# Revit family: Faucet-Lavatory-KOHLER-Forte-K-10270_1
name_source: partatom
category: Plumbing Fixtures
revit_build: Autodesk Revit 2015 (Build: 20140606_1530(x64)
units: mm (PartAtom-declared; Revit-internal decimal feet)

## types (6) — shared parameters
ADA Compliant = Yes
Assembly Code = D2010
CW Connection = Yes
Cold Water Inlet = Cold Water Inlet
Date Modified = 02/20/2019
Default Elevation = 36"
Drain Included = Yes
Faucet Hole Spacing = 4"
HW Connection = Yes
Handle Clearance = 2 9/16"
Height = 4 13/16"
Hot Water Inlet = Hot Water Inlet
Length = 5 1/8"
Manufacturer = KOHLER Co.
MasterFormat 1995 = 15410
MasterFormat 2004 = 22.41.39
Material = Premium Metal Construction
Pressure = 60.00 psi
Product Documentation Link = https://www.us.kohler.com
Product Name = Forté
Product Page URL = http://www.us.kohler.com
Spout Reach = 5 1/8"
URL = https://www.us.kohler.com
Vent Connection = No
Waste Connection = No
Waste Water Outlet = Waste Water Outlet
WaterSense Certified = Yes
Width = 4"

## per-type parameters (varying)
| type | Description | Finish | Flow Rate | Model | Sculpted Lever Handles | Traditional Lever Handles | Type |
| Sculpted Lever Handle, CP-Polished Chrome | Centerset bathroom sink faucet with sculpted lever handles | Kohler-Metal-CP-Polished_Chrome | 1 GPM | K-10270-4-CP | Yes | No | 1 |
| Sculpted Lever Handle, G-Brushed Chrome | Centerset bathroom sink faucet with sculpted lever handles | Kohler-Metal-G-Brushed_Chrome | 1 GPM | K-10270-4-G | Yes | No | 2 |
| Sculpted Lever Handle, BN-Vibrant Brushed Nickel | Centerset bathroom sink faucet with sculpted lever handles | Kohler-Metal-BN-Vibrant_Brushed_Nickel | 1 GPM | K-10270-4-BN | Yes | No | 3 |
| Traditional Lever Handle, CP-Polished Chrome | Centerset bathroom sink faucet with traditional lever handles | Kohler-Metal-CP-Polished_Chrome | 2 GPM | K-10270-4A-CP | No | Yes | 4 |
| Traditional Lever Handle, G-Brushed Chrome | Centerset bathroom sink faucet with traditional lever handles | Kohler-Metal-G-Brushed_Chrome | 2 GPM | K-10270-4A-G | No | Yes | 5 |
| Traditional Lever Handle, BN-Vibrant Brushed Nickel | Centerset bathroom sink faucet with traditional lever handles | Kohler-Metal-BN-Vibrant_Brushed_Nickel | 2 GPM | K-10270-4A-BN | No | Yes | 6 |

## geometry (parser evidence)
native form markers: Sweep x3
no freeform markers — native parametric forms only
